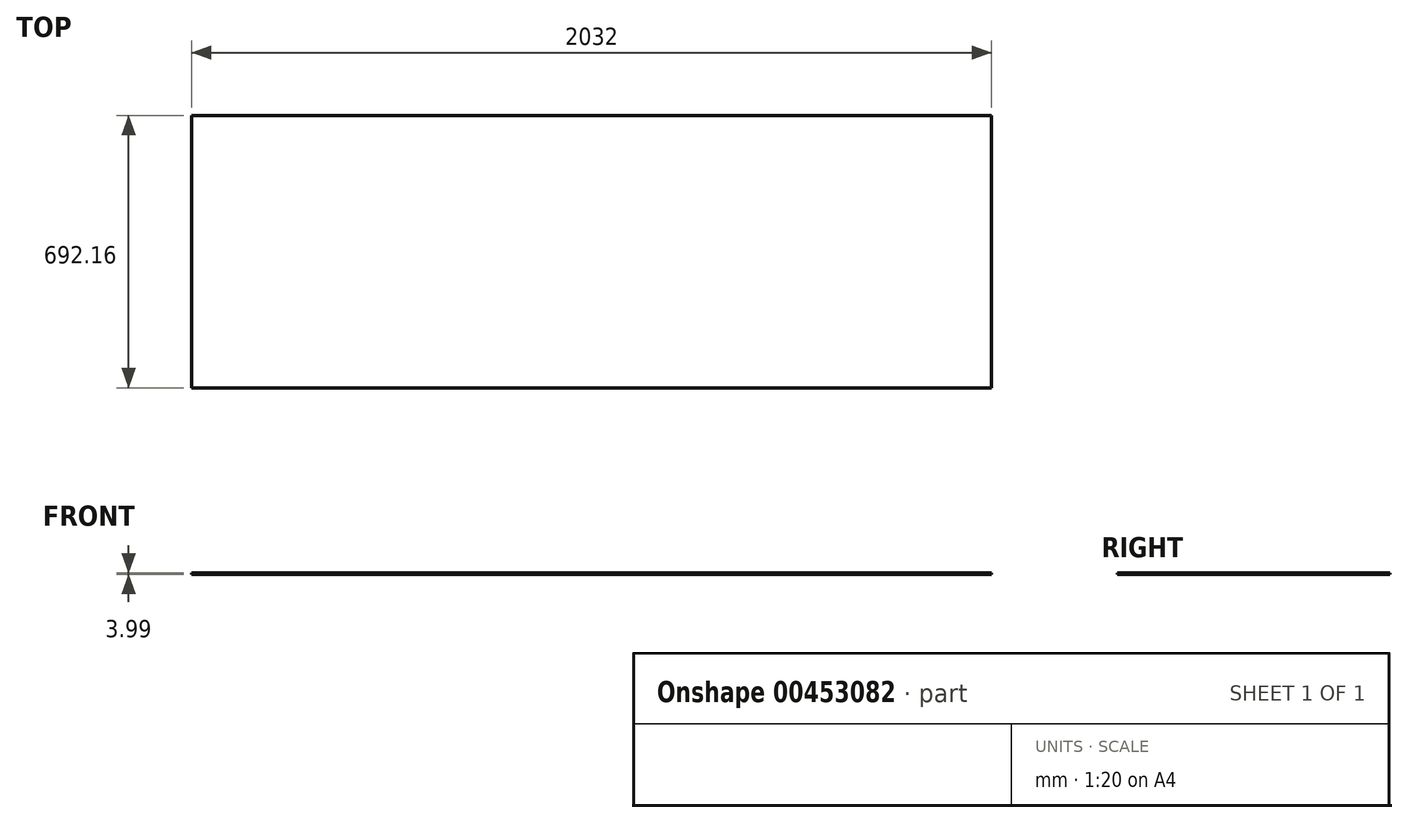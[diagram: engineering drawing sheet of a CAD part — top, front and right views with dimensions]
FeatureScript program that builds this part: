
annotation { "Feature Type Name" : "Feature", "Feature Type Description" : "" }
export const myFeature = defineFeature(function(context is Context, id is Id, definition is map)
    precondition{}
    {
        {
            var Q0;
            Q0=qCreatedBy(makeId("Top.planeOp"),FACE);
            var sketch = newSketch(context, id + "F0", { "sketchPlane" : qUnion([Q0])});
            skLineSegment(sketch, "E0.bottom", {"start": v(1016, 346.08) * mm, "end": v(-1016, 346.08) * mm});
            skLineSegment(sketch, "E0.top", {"start": v(1016, -346.08) * mm, "end": v(-1016, -346.08) * mm});
            skLineSegment(sketch, "E0.left", {"start": v(1016, 346.08) * mm, "end": v(1016, -346.07) * mm});
            skLineSegment(sketch, "E0.right", {"start": v(-1016, 346.08) * mm, "end": v(-1016, -346.08) * mm});
            skPoint(sketch, "E0.middle", {"position": v(0, 0) * mm});
            skSolve(sketch);
        }
        {
            var Q0;
            Q0 = qSketchRegion(id + "F0", true);
            extrude(context, id + "F1", {"entities" : qUnion([Q0]), "depth" : 4 * mm, "offsetDistance" : 25.4 * mm});
        }
    });
